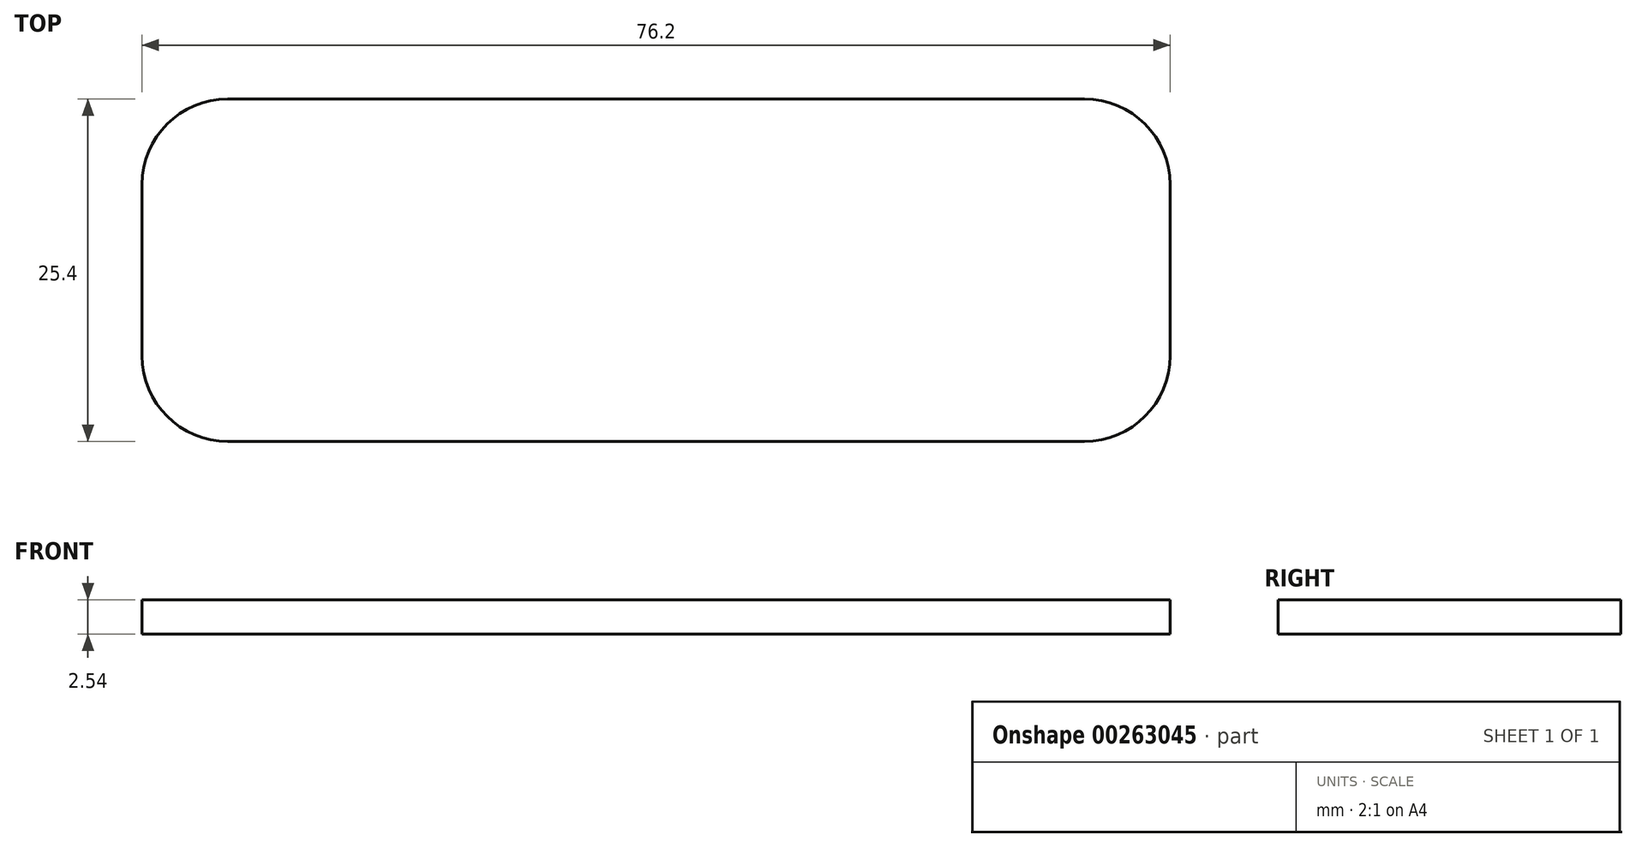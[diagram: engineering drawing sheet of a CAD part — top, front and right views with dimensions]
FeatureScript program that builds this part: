
annotation { "Feature Type Name" : "Feature", "Feature Type Description" : "" }
export const myFeature = defineFeature(function(context is Context, id is Id, definition is map)
    precondition{}
    {
        {
            var Q0;
            Q0=qCreatedBy(makeId("Top.planeOp"),FACE);
            var sketch = newSketch(context, id + "F0", { "sketchPlane" : qUnion([Q0])});
            skLineSegment(sketch, "E0.bottom", {"start": v(31.75, 12.7) * mm, "end": v(-31.75, 12.7) * mm});
            skLineSegment(sketch, "E0.top", {"start": v(31.75, -12.7) * mm, "end": v(-31.75, -12.7) * mm});
            skLineSegment(sketch, "E0.left", {"start": v(38.1, 6.35) * mm, "end": v(38.1, -6.35) * mm});
            skLineSegment(sketch, "E0.right", {"start": v(-38.1, 6.35) * mm, "end": v(-38.1, -6.35) * mm});
            skPoint(sketch, "E0.middle", {"position": v(0, 0) * mm});
            skPoint(sketch, "E1.visualSharp", {"position": v(-38.1, 12.7) * mm});
            skArc(sketch, "E1.filletArc", {"start": v(-31.75, 12.7) * mm, "mid": v(-36.24, 10.84) * mm, "end": v(-38.1, 6.35) * mm});
            skPoint(sketch, "E2.visualSharp", {"position": v(38.1, 12.7) * mm});
            skArc(sketch, "E2.filletArc", {"start": v(38.1, 6.35) * mm, "mid": v(36.24, 10.84) * mm, "end": v(31.75, 12.7) * mm});
            skPoint(sketch, "E3.visualSharp", {"position": v(38.1, -12.7) * mm});
            skArc(sketch, "E3.filletArc", {"start": v(31.75, -12.7) * mm, "mid": v(36.24, -10.84) * mm, "end": v(38.1, -6.35) * mm});
            skPoint(sketch, "E4.visualSharp", {"position": v(-38.1, -12.7) * mm});
            skArc(sketch, "E4.filletArc", {"start": v(-38.1, -6.35) * mm, "mid": v(-36.24, -10.84) * mm, "end": v(-31.75, -12.7) * mm});
            skSolve(sketch);
        }
        {
            var Q0;
            Q0 = qSketchRegion(id + "F0", true);
            extrude(context, id + "F1", {"entities" : qUnion([Q0]), "endBound" : BoundingType.SYMMETRIC, "depth" : 2.54 * mm});
        }
    });
